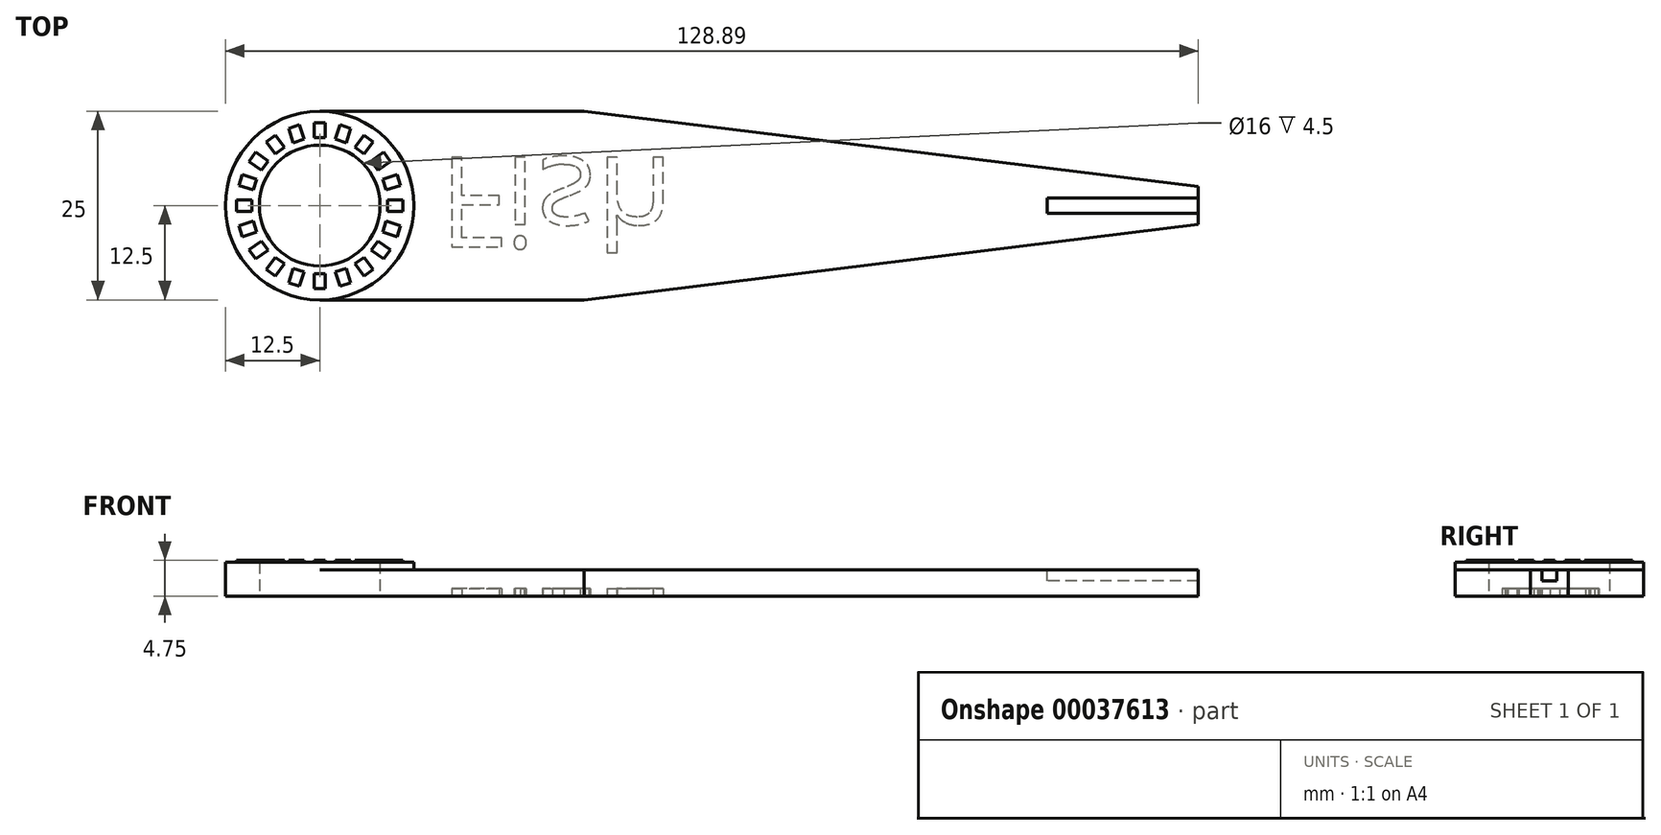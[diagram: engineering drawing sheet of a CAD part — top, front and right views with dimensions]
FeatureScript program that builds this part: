
annotation { "Feature Type Name" : "Feature", "Feature Type Description" : "" }
export const myFeature = defineFeature(function(context is Context, id is Id, definition is map)
    precondition{}
    {
        {
            var Q0;
            Q0=qCreatedBy(makeId("Top.planeOp"),FACE);
            var sketch = newSketch(context, id + "F0", { "sketchPlane" : qUnion([Q0])});
            skCircle(sketch, "E0", {"center": v(0, 0) * mm, "radius": 12.5 * mm});
            skCircle(sketch, "E1", {"center": v(0, 0) * mm, "radius": 8 * mm});
            skLineSegment(sketch, "E2", {"start": v(0, 12.5) * mm, "end": v(35, 12.5) * mm});
            skLineSegment(sketch, "E3", {"start": v(0, 0) * mm, "end": v(35.44, 0) * mm, "construction": true});
            skLineSegment(sketch, "E4.MirrorCS", {"start": v(0, -12.5) * mm, "end": v(35, -12.5) * mm});
            skLineSegment(sketch, "E5", {"start": v(35, 12.5) * mm, "end": v(116.39, 2.5) * mm});
            skLineSegment(sketch, "E6", {"start": v(35, 12.5) * mm, "end": v(96.18, 12.5) * mm, "construction": true});
            skLineSegment(sketch, "E7.MirrorCS", {"start": v(35, -12.5) * mm, "end": v(116.39, -2.5) * mm});
            skLineSegment(sketch, "E8", {"start": v(116.39, 2.5) * mm, "end": v(116.39, -2.5) * mm});
            skSolve(sketch);
        }
        {
            var Q0;
            Q0 = qSketchRegion(id + "F0", true);
            extrude(context, id + "F1", {"entities" : qUnion([Q0]), "depth" : 3.5 * mm});
        }
        {
            var Q0;
            Q0=makeQuery(id+"F1.opExtrude","CAP_FACE",FACE,{"disambiguationData":[OSD([sQuery(id+"F0.wireOp",EDGE,"E0"),sQuery(id+"F0.wireOp",EDGE,"E1"),sQuery(id+"F0.wireOp",EDGE,"E2"),sQuery(id+"F0.wireOp",EDGE,"E4.MirrorCS"),sQuery(id+"F0.wireOp",EDGE,"E5"),sQuery(id+"F0.wireOp",EDGE,"E7.MirrorCS"),sQuery(id+"F0.wireOp",EDGE,"E8")])],"isStart":false});
            var sketch = newSketch(context, id + "F2", { "sketchPlane" : qUnion([Q0])});
            skCircle(sketch, "E9", {"center": v(0, 0) * mm, "radius": 8 * mm});
            skCircle(sketch, "E10", {"center": v(0, 0) * mm, "radius": 12.5 * mm});
            skSolve(sketch);
        }
        {
            var Q0;
            Q0 = qSketchRegion(id + "F2", true);
            extrude(context, id + "F3", {"entities" : qUnion([Q0]), "operationType" : NewBodyOperationType.ADD, "depth" : 1 * mm});
        }
        {
            var Q0;
            Q0=makeQuery(id+"F3.opExtrude","CAP_FACE",FACE,{"disambiguationData":[OSD([sQuery(id+"F2.wireOp",EDGE,"E9"),sQuery(id+"F2.wireOp",EDGE,"E10")])],"isStart":false});
            var sketch = newSketch(context, id + "F4", { "sketchPlane" : qUnion([Q0])});
            skLineSegment(sketch, "E11.bottom", {"start": v(-0.75, 11) * mm, "end": v(0.75, 11) * mm});
            skLineSegment(sketch, "E11.top", {"start": v(-0.75, 9) * mm, "end": v(0.75, 9) * mm});
            skLineSegment(sketch, "E11.left", {"start": v(-0.75, 11) * mm, "end": v(-0.75, 9) * mm});
            skLineSegment(sketch, "E11.right", {"start": v(0.75, 11) * mm, "end": v(0.75, 9) * mm});
            skPoint(sketch, "E12", {"position": v(0, 8) * mm});
            skLineSegment(sketch, "E13.1.0", {"start": v(-4.11, 10.23) * mm, "end": v(-2.69, 10.7) * mm});
            skLineSegment(sketch, "E13.1.1", {"start": v(-2.69, 10.7) * mm, "end": v(-2.07, 8.8) * mm});
            skLineSegment(sketch, "E13.1.2", {"start": v(-3.5, 8.33) * mm, "end": v(-2.07, 8.8) * mm});
            skLineSegment(sketch, "E13.1.3", {"start": v(-4.11, 10.23) * mm, "end": v(-3.5, 8.33) * mm});
            skLineSegment(sketch, "E13.2.0", {"start": v(-7.07, 8.46) * mm, "end": v(-5.86, 9.34) * mm});
            skLineSegment(sketch, "E13.2.1", {"start": v(-5.86, 9.34) * mm, "end": v(-4.68, 7.72) * mm});
            skLineSegment(sketch, "E13.2.2", {"start": v(-5.9, 6.84) * mm, "end": v(-4.68, 7.72) * mm});
            skLineSegment(sketch, "E13.2.3", {"start": v(-7.07, 8.46) * mm, "end": v(-5.9, 6.84) * mm});
            skLineSegment(sketch, "E13.3.0", {"start": v(-9.34, 5.86) * mm, "end": v(-8.46, 7.07) * mm});
            skLineSegment(sketch, "E13.3.1", {"start": v(-8.46, 7.07) * mm, "end": v(-6.84, 5.9) * mm});
            skLineSegment(sketch, "E13.3.2", {"start": v(-7.72, 4.68) * mm, "end": v(-6.84, 5.9) * mm});
            skLineSegment(sketch, "E13.3.3", {"start": v(-9.34, 5.86) * mm, "end": v(-7.72, 4.68) * mm});
            skLineSegment(sketch, "E13.4.0", {"start": v(-10.7, 2.69) * mm, "end": v(-10.23, 4.11) * mm});
            skLineSegment(sketch, "E13.4.1", {"start": v(-10.23, 4.11) * mm, "end": v(-8.33, 3.5) * mm});
            skLineSegment(sketch, "E13.4.2", {"start": v(-8.8, 2.07) * mm, "end": v(-8.33, 3.5) * mm});
            skLineSegment(sketch, "E13.4.3", {"start": v(-10.7, 2.69) * mm, "end": v(-8.8, 2.07) * mm});
            skLineSegment(sketch, "E13.5.0", {"start": v(-11, -0.75) * mm, "end": v(-11, 0.75) * mm});
            skLineSegment(sketch, "E13.5.1", {"start": v(-11, 0.75) * mm, "end": v(-9, 0.75) * mm});
            skLineSegment(sketch, "E13.5.2", {"start": v(-9, -0.75) * mm, "end": v(-9, 0.75) * mm});
            skLineSegment(sketch, "E13.5.3", {"start": v(-11, -0.75) * mm, "end": v(-9, -0.75) * mm});
            skLineSegment(sketch, "E13.6.0", {"start": v(-10.23, -4.11) * mm, "end": v(-10.7, -2.69) * mm});
            skLineSegment(sketch, "E13.6.1", {"start": v(-10.7, -2.69) * mm, "end": v(-8.8, -2.07) * mm});
            skLineSegment(sketch, "E13.6.2", {"start": v(-8.33, -3.5) * mm, "end": v(-8.8, -2.07) * mm});
            skLineSegment(sketch, "E13.6.3", {"start": v(-10.23, -4.11) * mm, "end": v(-8.33, -3.5) * mm});
            skLineSegment(sketch, "E13.7.0", {"start": v(-8.46, -7.07) * mm, "end": v(-9.34, -5.86) * mm});
            skLineSegment(sketch, "E13.7.1", {"start": v(-9.34, -5.86) * mm, "end": v(-7.72, -4.68) * mm});
            skLineSegment(sketch, "E13.7.2", {"start": v(-6.84, -5.9) * mm, "end": v(-7.72, -4.68) * mm});
            skLineSegment(sketch, "E13.7.3", {"start": v(-8.46, -7.07) * mm, "end": v(-6.84, -5.9) * mm});
            skLineSegment(sketch, "E13.8.0", {"start": v(-5.86, -9.34) * mm, "end": v(-7.07, -8.46) * mm});
            skLineSegment(sketch, "E13.8.1", {"start": v(-7.07, -8.46) * mm, "end": v(-5.9, -6.84) * mm});
            skLineSegment(sketch, "E13.8.2", {"start": v(-4.68, -7.72) * mm, "end": v(-5.9, -6.84) * mm});
            skLineSegment(sketch, "E13.8.3", {"start": v(-5.86, -9.34) * mm, "end": v(-4.68, -7.72) * mm});
            skLineSegment(sketch, "E13.9.0", {"start": v(-2.69, -10.7) * mm, "end": v(-4.11, -10.23) * mm});
            skLineSegment(sketch, "E13.9.1", {"start": v(-4.11, -10.23) * mm, "end": v(-3.5, -8.33) * mm});
            skLineSegment(sketch, "E13.9.2", {"start": v(-2.07, -8.8) * mm, "end": v(-3.5, -8.33) * mm});
            skLineSegment(sketch, "E13.9.3", {"start": v(-2.69, -10.7) * mm, "end": v(-2.07, -8.8) * mm});
            skLineSegment(sketch, "E13.10.0", {"start": v(0.75, -11) * mm, "end": v(-0.75, -11) * mm});
            skLineSegment(sketch, "E13.10.1", {"start": v(-0.75, -11) * mm, "end": v(-0.75, -9) * mm});
            skLineSegment(sketch, "E13.10.2", {"start": v(0.75, -9) * mm, "end": v(-0.75, -9) * mm});
            skLineSegment(sketch, "E13.10.3", {"start": v(0.75, -11) * mm, "end": v(0.75, -9) * mm});
            skLineSegment(sketch, "E13.11.0", {"start": v(4.11, -10.23) * mm, "end": v(2.69, -10.7) * mm});
            skLineSegment(sketch, "E13.11.1", {"start": v(2.69, -10.7) * mm, "end": v(2.07, -8.8) * mm});
            skLineSegment(sketch, "E13.11.2", {"start": v(3.5, -8.33) * mm, "end": v(2.07, -8.8) * mm});
            skLineSegment(sketch, "E13.11.3", {"start": v(4.11, -10.23) * mm, "end": v(3.5, -8.33) * mm});
            skLineSegment(sketch, "E13.12.0", {"start": v(7.07, -8.46) * mm, "end": v(5.86, -9.34) * mm});
            skLineSegment(sketch, "E13.12.1", {"start": v(5.86, -9.34) * mm, "end": v(4.68, -7.72) * mm});
            skLineSegment(sketch, "E13.12.2", {"start": v(5.9, -6.84) * mm, "end": v(4.68, -7.72) * mm});
            skLineSegment(sketch, "E13.12.3", {"start": v(7.07, -8.46) * mm, "end": v(5.9, -6.84) * mm});
            skLineSegment(sketch, "E13.13.0", {"start": v(9.34, -5.86) * mm, "end": v(8.46, -7.07) * mm});
            skLineSegment(sketch, "E13.13.1", {"start": v(8.46, -7.07) * mm, "end": v(6.84, -5.9) * mm});
            skLineSegment(sketch, "E13.13.2", {"start": v(7.72, -4.68) * mm, "end": v(6.84, -5.9) * mm});
            skLineSegment(sketch, "E13.13.3", {"start": v(9.34, -5.86) * mm, "end": v(7.72, -4.68) * mm});
            skLineSegment(sketch, "E13.14.0", {"start": v(10.7, -2.69) * mm, "end": v(10.23, -4.11) * mm});
            skLineSegment(sketch, "E13.14.1", {"start": v(10.23, -4.11) * mm, "end": v(8.33, -3.5) * mm});
            skLineSegment(sketch, "E13.14.2", {"start": v(8.8, -2.07) * mm, "end": v(8.33, -3.5) * mm});
            skLineSegment(sketch, "E13.14.3", {"start": v(10.7, -2.69) * mm, "end": v(8.8, -2.07) * mm});
            skLineSegment(sketch, "E13.15.0", {"start": v(11, 0.75) * mm, "end": v(11, -0.75) * mm});
            skLineSegment(sketch, "E13.15.1", {"start": v(11, -0.75) * mm, "end": v(9, -0.75) * mm});
            skLineSegment(sketch, "E13.15.2", {"start": v(9, 0.75) * mm, "end": v(9, -0.75) * mm});
            skLineSegment(sketch, "E13.15.3", {"start": v(11, 0.75) * mm, "end": v(9, 0.75) * mm});
            skLineSegment(sketch, "E13.16.0", {"start": v(10.23, 4.11) * mm, "end": v(10.7, 2.69) * mm});
            skLineSegment(sketch, "E13.16.1", {"start": v(10.7, 2.69) * mm, "end": v(8.8, 2.07) * mm});
            skLineSegment(sketch, "E13.16.2", {"start": v(8.33, 3.5) * mm, "end": v(8.8, 2.07) * mm});
            skLineSegment(sketch, "E13.16.3", {"start": v(10.23, 4.11) * mm, "end": v(8.33, 3.5) * mm});
            skLineSegment(sketch, "E13.17.0", {"start": v(8.46, 7.07) * mm, "end": v(9.34, 5.86) * mm});
            skLineSegment(sketch, "E13.17.1", {"start": v(9.34, 5.86) * mm, "end": v(7.72, 4.68) * mm});
            skLineSegment(sketch, "E13.17.2", {"start": v(6.84, 5.9) * mm, "end": v(7.72, 4.68) * mm});
            skLineSegment(sketch, "E13.17.3", {"start": v(8.46, 7.07) * mm, "end": v(6.84, 5.9) * mm});
            skLineSegment(sketch, "E13.18.0", {"start": v(5.86, 9.34) * mm, "end": v(7.07, 8.46) * mm});
            skLineSegment(sketch, "E13.18.1", {"start": v(7.07, 8.46) * mm, "end": v(5.9, 6.84) * mm});
            skLineSegment(sketch, "E13.18.2", {"start": v(4.68, 7.72) * mm, "end": v(5.9, 6.84) * mm});
            skLineSegment(sketch, "E13.18.3", {"start": v(5.86, 9.34) * mm, "end": v(4.68, 7.72) * mm});
            skLineSegment(sketch, "E13.19.0", {"start": v(2.69, 10.7) * mm, "end": v(4.11, 10.23) * mm});
            skLineSegment(sketch, "E13.19.1", {"start": v(4.11, 10.23) * mm, "end": v(3.5, 8.33) * mm});
            skLineSegment(sketch, "E13.19.2", {"start": v(2.07, 8.8) * mm, "end": v(3.5, 8.33) * mm});
            skLineSegment(sketch, "E13.19.3", {"start": v(2.69, 10.7) * mm, "end": v(2.07, 8.8) * mm});
            skPoint(sketch, "E13.center", {"position": v(0, 0) * mm});
            skSolve(sketch);
        }
        {
            var Q0;
            Q0 = qSketchRegion(id + "F4", true);
            extrude(context, id + "F5", {"entities" : qUnion([Q0]), "operationType" : NewBodyOperationType.ADD, "depth" : .25 * mm});
        }
        {
            var Q0;
            Q0=makeQuery(id+"F1.opExtrude","CAP_FACE",FACE,{"disambiguationData":[OSD([sQuery(id+"F0.wireOp",EDGE,"E0"),sQuery(id+"F0.wireOp",EDGE,"E1"),sQuery(id+"F0.wireOp",EDGE,"E2"),sQuery(id+"F0.wireOp",EDGE,"E4.MirrorCS"),sQuery(id+"F0.wireOp",EDGE,"E5"),sQuery(id+"F0.wireOp",EDGE,"E7.MirrorCS"),sQuery(id+"F0.wireOp",EDGE,"E8")])],"isStart":false});
            var sketch = newSketch(context, id + "F6", { "sketchPlane" : qUnion([Q0])});
            skLineSegment(sketch, "E14.bottom", {"start": v(116.39, 1) * mm, "end": v(96.39, 1) * mm});
            skLineSegment(sketch, "E14.top", {"start": v(116.39, -1) * mm, "end": v(96.39, -1) * mm});
            skLineSegment(sketch, "E14.left", {"start": v(116.39, 1) * mm, "end": v(116.39, -1) * mm});
            skLineSegment(sketch, "E14.right", {"start": v(96.39, 1) * mm, "end": v(96.39, -1) * mm});
            skSolve(sketch);
        }
        {
            var Q0;
            Q0 = qSketchRegion(id + "F6", true);
            extrude(context, id + "F7", {"entities" : qUnion([Q0]), "operationType" : NewBodyOperationType.REMOVE, "oppositeDirection" : true, "depth" : 1.5 * mm});
        }
        {
            var Q0;
            Q0=makeQuery(id+"F1.opExtrude","CAP_FACE",FACE,{"disambiguationData":[OSD([sQuery(id+"F0.wireOp",EDGE,"E0"),sQuery(id+"F0.wireOp",EDGE,"E1"),sQuery(id+"F0.wireOp",EDGE,"E2"),sQuery(id+"F0.wireOp",EDGE,"E4.MirrorCS"),sQuery(id+"F0.wireOp",EDGE,"E5"),sQuery(id+"F0.wireOp",EDGE,"E7.MirrorCS"),sQuery(id+"F0.wireOp",EDGE,"E8")])],"isStart":true});
            var sketch = newSketch(context, id + "F8", { "sketchPlane" : qUnion([Q0])});
            skText(sketch, "E15", { "text": "Fish\n", "fontName": "OpenSans-Regular.ttf"});
            const initialGuessF8  = {"E15": [0.01584, -0.00643, 1, 0, 0.012]};
            skSetInitialGuess(sketch, initialGuessF8);
            skSolve(sketch);
        }
        {
            var Q0;
            Q0 = qSketchRegion(id + "F8", true);
            extrude(context, id + "F9", {"entities" : qUnion([Q0]), "operationType" : NewBodyOperationType.REMOVE, "oppositeDirection" : true, "depth" : 1 * mm});
        }
    });
